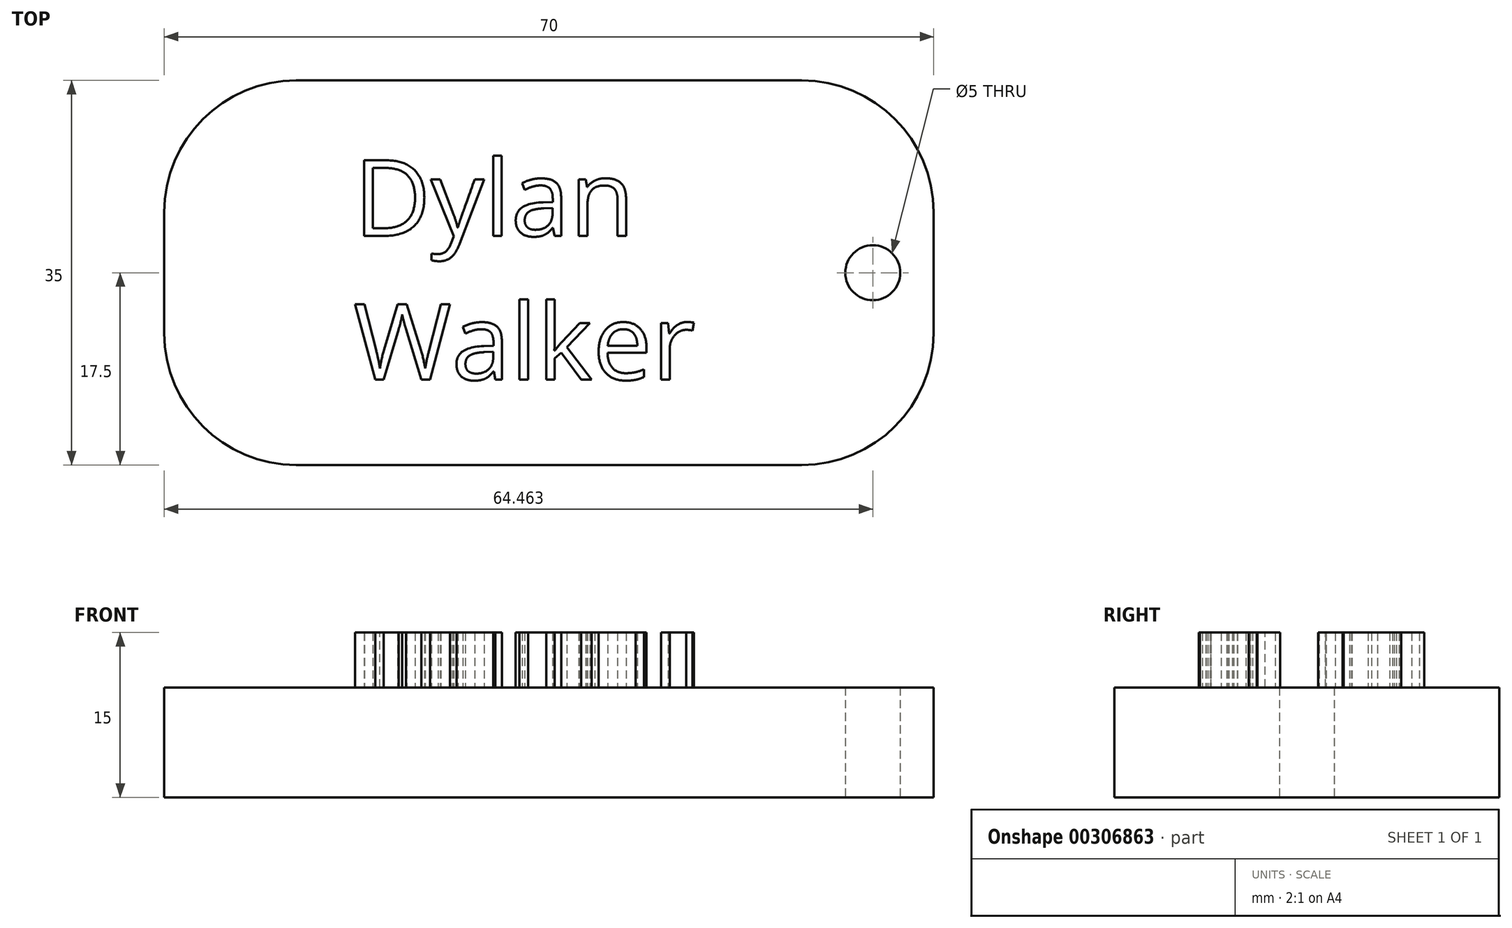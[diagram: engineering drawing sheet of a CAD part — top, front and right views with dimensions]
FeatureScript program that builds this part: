
annotation { "Feature Type Name" : "Feature", "Feature Type Description" : "" }
export const myFeature = defineFeature(function(context is Context, id is Id, definition is map)
    precondition{}
    {
        {
            var Q0;
            Q0=qCreatedBy(makeId("Top.planeOp"),FACE);
            var sketch = newSketch(context, id + "F0", { "sketchPlane" : qUnion([Q0])});
            skLineSegment(sketch, "E0.bottom", {"start": v(37.6, 17.5) * mm, "end": v(-32.4, 17.5) * mm});
            skLineSegment(sketch, "E0.top", {"start": v(37.6, -17.5) * mm, "end": v(-32.4, -17.5) * mm});
            skLineSegment(sketch, "E0.left", {"start": v(37.6, 17.5) * mm, "end": v(37.6, -17.5) * mm});
            skLineSegment(sketch, "E0.right", {"start": v(-32.4, 17.5) * mm, "end": v(-32.4, -17.5) * mm});
            skSolve(sketch);
        }
        {
            var Q0;
            Q0=makeQuery(id+"F0.imprint","IMPRINT",FACE,{"disambiguationData":[TD([[makeQuery(id+"F0.imprint","IMPRINT",EDGE,{"derivedFrom":sQuery(id+"F0.wireOp",EDGE,"E0.bottom")}),1.0]])]});
            extrude(context, id + "F1", {"entities" : qUnion([Q0]), "depth" : 10 * mm});
        }
        {
            var Q0;
            Q0=makeQuery(id+"F1.opExtrude","SWEPT_EDGE",EDGE,{"disambiguationData":[OSD([sQuery(id+"F0.wireOp",EDGE,"E0.top"),sQuery(id+"F0.wireOp",EDGE,"E0.left")])]});
            var Q1;
            Q1=makeQuery(id+"F1.opExtrude","SWEPT_EDGE",EDGE,{"disambiguationData":[OSD([sQuery(id+"F0.wireOp",EDGE,"E0.bottom"),sQuery(id+"F0.wireOp",EDGE,"E0.left")])]});
            var Q2;
            Q2=makeQuery(id+"F1.opExtrude","SWEPT_EDGE",EDGE,{"disambiguationData":[OSD([sQuery(id+"F0.wireOp",EDGE,"E0.top"),sQuery(id+"F0.wireOp",EDGE,"E0.right")])]});
            var Q3;
            Q3=makeQuery(id+"F1.opExtrude","SWEPT_EDGE",EDGE,{"disambiguationData":[OSD([sQuery(id+"F0.wireOp",EDGE,"E0.bottom"),sQuery(id+"F0.wireOp",EDGE,"E0.right")])]});
            fillet(context, id + "F2", {"entities" : qUnion([Q0, Q1, Q2, Q3]), "radius" : 12 * mm, "tangentPropagation" : true, "allowEdgeOverflow" : false});
        }
        {
            var Q0;
            Q0=makeQuery(id+"F1.opExtrude","CAP_FACE",FACE,{"disambiguationData":[OSD([sQuery(id+"F0.wireOp",EDGE,"E0.bottom"),sQuery(id+"F0.wireOp",EDGE,"E0.top"),sQuery(id+"F0.wireOp",EDGE,"E0.left"),sQuery(id+"F0.wireOp",EDGE,"E0.right")])],"isStart":false});
            var sketch = newSketch(context, id + "F3", { "sketchPlane" : qUnion([Q0])});
            skText(sketch, "E1", { "text": "Dylan\nWalker", "fontName": "OpenSans-Regular.ttf"});
            const initialGuessF3  = {"E1": [-0.01517, 0.00336, 1, 0, 0.00693]};
            skSetInitialGuess(sketch, initialGuessF3);
            skSolve(sketch);
        }
        {
            var Q0;
            Q0=qCreatedBy(makeId("Top.planeOp"),FACE);
            var sketch = newSketch(context, id + "F4", { "sketchPlane" : qUnion([Q0])});
            skPoint(sketch, "E2", {"position": v(32.06, 0) * mm});
            skSolve(sketch);
        }
        {
            var Q0;
            Q0=sQuery(id+"F4.wireOp",VERTEX,"E2");
            var Q1;
            Q1=makeQuery(id+"F1.opExtrude","SWEPT_BODY",BODY,{"disambiguationData":[OSD([sQuery(id+"F0.wireOp",EDGE,"E0.bottom"),sQuery(id+"F0.wireOp",EDGE,"E0.top"),sQuery(id+"F0.wireOp",EDGE,"E0.left"),sQuery(id+"F0.wireOp",EDGE,"E0.right")])]});
            hole(context, id + "F5", {"style" : HoleStyle.SIMPLE, "endStyle" : HoleEndStyle.THROUGH, "oppositeDirection" : true, "holeDiameter" : 5 * mm, "tappedDepth" : 12 * mm, "tapClearance" : 3, "locations" : qUnion([Q0]), "scope" : qUnion([Q1])});
        }
        {
            var Q0;
            Q0 = qSketchRegion(id + "F3", true);
            extrude(context, id + "F6", {"entities" : qUnion([Q0]), "operationType" : NewBodyOperationType.ADD, "depth" : 5 * mm});
        }
    });
